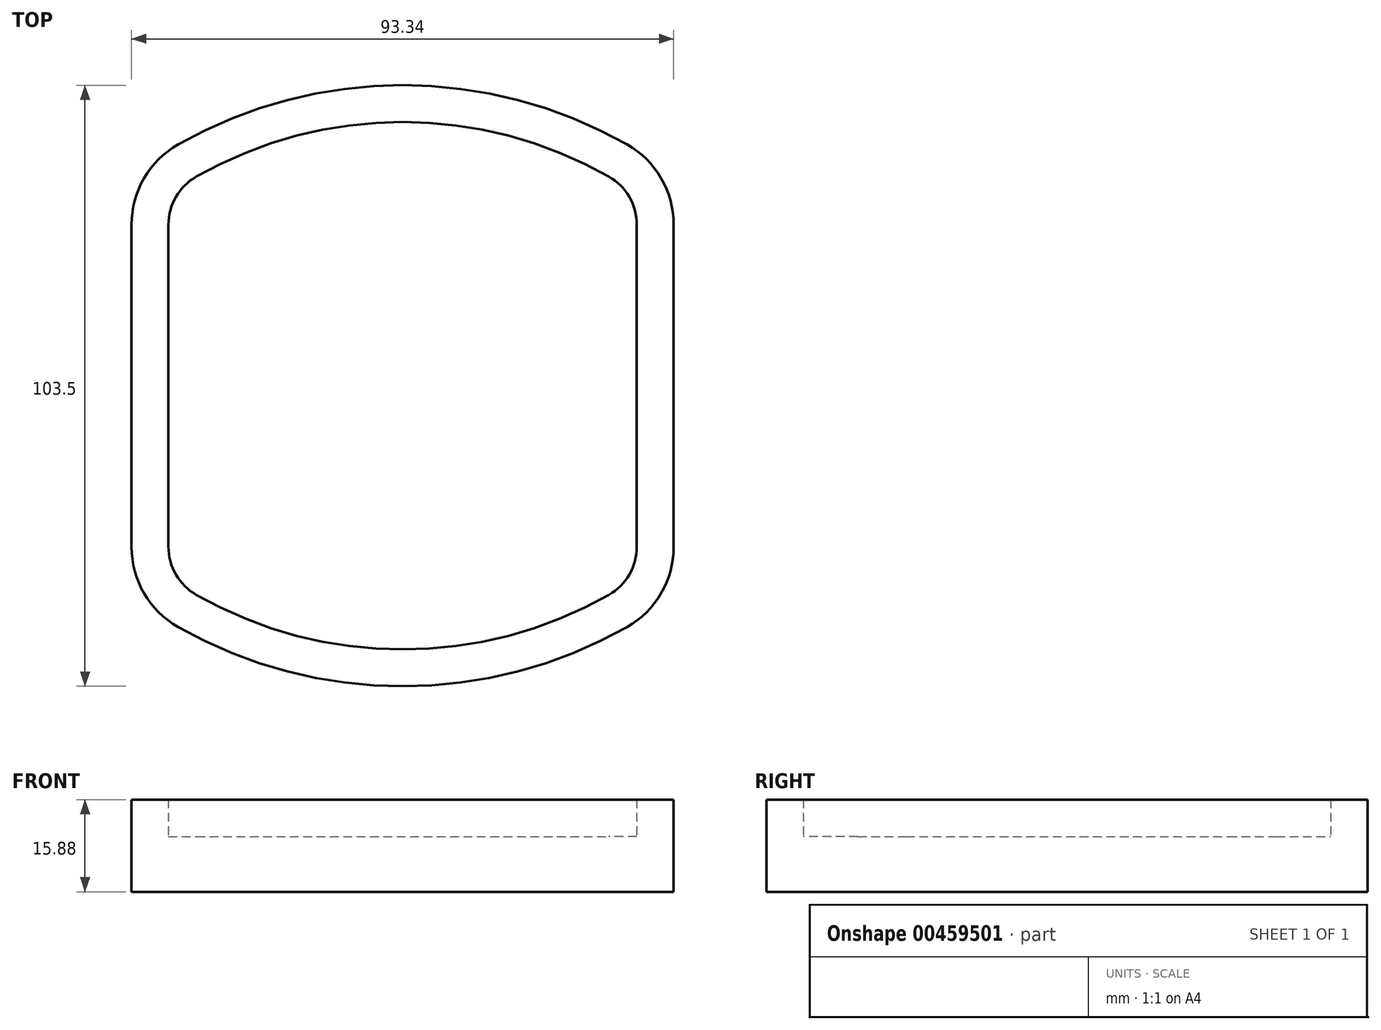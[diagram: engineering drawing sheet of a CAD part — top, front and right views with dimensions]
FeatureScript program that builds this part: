
annotation { "Feature Type Name" : "Feature", "Feature Type Description" : "" }
export const myFeature = defineFeature(function(context is Context, id is Id, definition is map)
    precondition{}
    {
        {
            var Q0;
            Q0=qCreatedBy(makeId("Top.planeOp"),FACE);
            var sketch = newSketch(context, id + "F0", { "sketchPlane" : qUnion([Q0])});
            skLineSegment(sketch, "E0", {"start": v(-40.32, -27.74) * mm, "end": v(-40.32, 27.74) * mm});
            skLineSegment(sketch, "E1.0", {"start": v(40.32, -27.74) * mm, "end": v(40.32, 27.74) * mm});
            skLineSegment(sketch, "E2", {"start": v(-40.32, 0) * mm, "end": v(40.32, 0) * mm, "construction": true});
            skLineSegment(sketch, "E3.0", {"start": v(-40.32, 33.02) * mm, "end": v(40.32, 33.02) * mm, "construction": true});
            skLineSegment(sketch, "E4.0", {"start": v(-40.32, -33.02) * mm, "end": v(40.32, -33.02) * mm, "construction": true});
            skArc(sketch, "E5", {"start": v(35.5, 36.02) * mm, "mid": v(0, 45.4) * mm, "end": v(-35.5, 36.02) * mm});
            skPoint(sketch, "E5.third.point", {"position": v(0, 45.4) * mm});
            skArc(sketch, "E6", {"start": v(-35.5, -36.02) * mm, "mid": v(0, -45.4) * mm, "end": v(35.5, -36.02) * mm});
            skPoint(sketch, "E6.third.point", {"position": v(0, -45.4) * mm});
            skPoint(sketch, "E7.visualSharp", {"position": v(-40.32, 33.02) * mm});
            skArc(sketch, "E7.filletArc", {"start": v(-35.5, 36.02) * mm, "mid": v(-39.03, 32.53) * mm, "end": v(-40.32, 27.74) * mm});
            skPoint(sketch, "E8.visualSharp", {"position": v(40.32, 33.02) * mm});
            skArc(sketch, "E8.filletArc", {"start": v(40.32, 27.74) * mm, "mid": v(39.03, 32.53) * mm, "end": v(35.5, 36.02) * mm});
            skPoint(sketch, "E9.visualSharp", {"position": v(40.32, -33.02) * mm});
            skArc(sketch, "E9.filletArc", {"start": v(35.5, -36.02) * mm, "mid": v(39.03, -32.53) * mm, "end": v(40.32, -27.74) * mm});
            skPoint(sketch, "E10.visualSharp", {"position": v(-40.32, -33.02) * mm});
            skArc(sketch, "E10.filletArc", {"start": v(-40.32, -27.74) * mm, "mid": v(-39.03, -32.53) * mm, "end": v(-35.5, -36.02) * mm});
            skLineSegment(sketch, "E11", {"start": v(0, 45.4) * mm, "end": v(0, -45.4) * mm, "construction": true});
            skArc(sketch, "E12.0", {"start": v(46.67, 27.74) * mm, "mid": v(44.52, 35.72) * mm, "end": v(38.64, 41.54) * mm});
            skLineSegment(sketch, "E12.1", {"start": v(46.67, -27.74) * mm, "end": v(46.67, 27.74) * mm});
            skArc(sketch, "E12.2", {"start": v(38.64, 41.54) * mm, "mid": v(0, 51.75) * mm, "end": v(-38.64, 41.54) * mm});
            skArc(sketch, "E12.3", {"start": v(38.64, -41.54) * mm, "mid": v(44.52, -35.72) * mm, "end": v(46.67, -27.74) * mm});
            skArc(sketch, "E12.4", {"start": v(-38.64, 41.54) * mm, "mid": v(-44.52, 35.72) * mm, "end": v(-46.67, 27.74) * mm});
            skLineSegment(sketch, "E12.5", {"start": v(-46.67, -27.74) * mm, "end": v(-46.67, 27.74) * mm});
            skArc(sketch, "E12.6", {"start": v(-46.67, -27.74) * mm, "mid": v(-44.52, -35.72) * mm, "end": v(-38.64, -41.54) * mm});
            skArc(sketch, "E12.7", {"start": v(-38.64, -41.54) * mm, "mid": v(0, -51.75) * mm, "end": v(38.64, -41.54) * mm});
            skSolve(sketch);
        }
        {
            var Q0;
            Q0 = qSketchRegion(id + "F0", true);
            extrude(context, id + "F1", {"entities" : qUnion([Q0]), "depth" : 6.35 * mm});
        }
        {
            var Q0;
            Q0=qCreatedBy(makeId("Top.planeOp"),FACE);
            var sketch = newSketch(context, id + "F2", { "sketchPlane" : qUnion([Q0])});
            skLineSegment(sketch, "E13.0", {"start": v(46.67, -27.74) * mm, "end": v(46.67, 27.74) * mm});
            skArc(sketch, "E14.0", {"start": v(38.64, -41.54) * mm, "mid": v(44.52, -35.72) * mm, "end": v(46.67, -27.74) * mm});
            skArc(sketch, "E15.0", {"start": v(-38.64, -41.54) * mm, "mid": v(0, -51.75) * mm, "end": v(38.64, -41.54) * mm});
            skPoint(sketch, "E16.0", {"position": v(-44.52, -35.72) * mm});
            skLineSegment(sketch, "E17.0", {"start": v(-46.67, -27.74) * mm, "end": v(-46.67, 27.74) * mm});
            skPoint(sketch, "E18.0", {"position": v(-44.52, 35.72) * mm});
            skArc(sketch, "E19.0", {"start": v(38.64, 41.54) * mm, "mid": v(0, 51.75) * mm, "end": v(-38.64, 41.54) * mm});
            skArc(sketch, "E20.0", {"start": v(46.67, 27.74) * mm, "mid": v(44.52, 35.72) * mm, "end": v(38.64, 41.54) * mm});
            skArc(sketch, "E21.0", {"start": v(-38.64, 41.54) * mm, "mid": v(-44.52, 35.72) * mm, "end": v(-46.67, 27.74) * mm});
            skArc(sketch, "E22.0", {"start": v(-46.67, -27.74) * mm, "mid": v(-44.52, -35.72) * mm, "end": v(-38.64, -41.54) * mm});
            skSolve(sketch);
        }
        {
            var Q0;
            Q0 = qSketchRegion(id + "F2", true);
            extrude(context, id + "F3", {"entities" : qUnion([Q0]), "operationType" : NewBodyOperationType.ADD, "oppositeDirection" : true, "depth" : 9.52 * mm});
        }
    });
